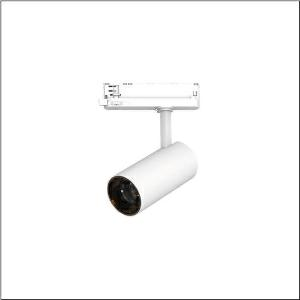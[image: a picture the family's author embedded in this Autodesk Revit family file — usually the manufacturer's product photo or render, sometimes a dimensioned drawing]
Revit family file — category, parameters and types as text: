
# Revit family: spot_31_slim_51sf127fa2b
name_source: partatom
category: Lighting Fixtures
units: mm (PartAtom-declared; Revit-internal decimal feet)

## family parameters
Cut with Voids When Loaded = No
Host = Face
Light Source = No
Part Type = Normal
Room Calculation Point = No
Round Connector Dimension = Use Diameter
Shared = No

## types (1)
- Spot 31 Slim (1 x LED, 2090 lm, 16.3 W, 2700K)
    Apparent Load = 16 VA
    CIE Flux Codes = 94 98 99 100 100
    Color Rendering = 90
    Color Temperature = 2700K
    Default Elevation = 1800 mm
    Description = Spot 31 Slim, directional spotlight, light control with reflector, of aluminium, LED rated luminous flux: 2.100lm, light colour: 927, control gear: ECG, with 3-phase adapter, mains connection: 220..240V, AC, 50/60Hz, housing, of aluminium, traffic white (RAL 9016), diameter: 70mm, adapter, of plastic, protection rating (complete): IP20, insulation class (complete): insulation class I (protective earthing), certification: CE, impact resistance: IK02, packaging unit: 1 piece
    Height = 210 mm
    Lamp = 1 x LED
    Lamp Light Flux = 2090 lm
    Lamp Power = 16.3 W
    Lamp count = 1
    Length = 70 mm
    Luminous efficacy = 128 lm/W
    Manufacturer = Siteco
    ModVariant = No
    Model = 51SF127FA2B
    Mounting Place = Ceiling
    Mounting Type = Pendant
    Number of Poles = 1
    OnlyDefault = Yes
    Power Factor = 1
    Product Name = Spot 31 Slim
    Product group = directional spotlight
    ProductGroupID = 905
    Protection Class = Protection class I
    Protection Degree = IP 20
    RLX_Detail_Level = 1
    RLX_Emergency_Light_Flux = 0 lm
    RLX_Emergency_Type = 0
    RLX_Emergency_Type_DB = No
    RlxData = <blob elided: 14169 chars, md5=cf3c51cd>
    Socket = socket
    Standby Power = 0 W
    System Light Flux = 2090 lm
    System Power = 16 W
    Type Comments = Product without accessories
    Type Image = l_1228468.jpg
    URL = http://relux.com
    VarID = ---
    Voltage = 0 V
    Weight = 0.00 kg
    Width = 0 mm  [stored 0 ft]

note: [stored X ft] marks values corroborated as IEEE doubles in the binary element streams (Revit-internal decimal feet)

## geometry (parser evidence)
native form markers: Sweep x11
no freeform markers — native parametric forms only
